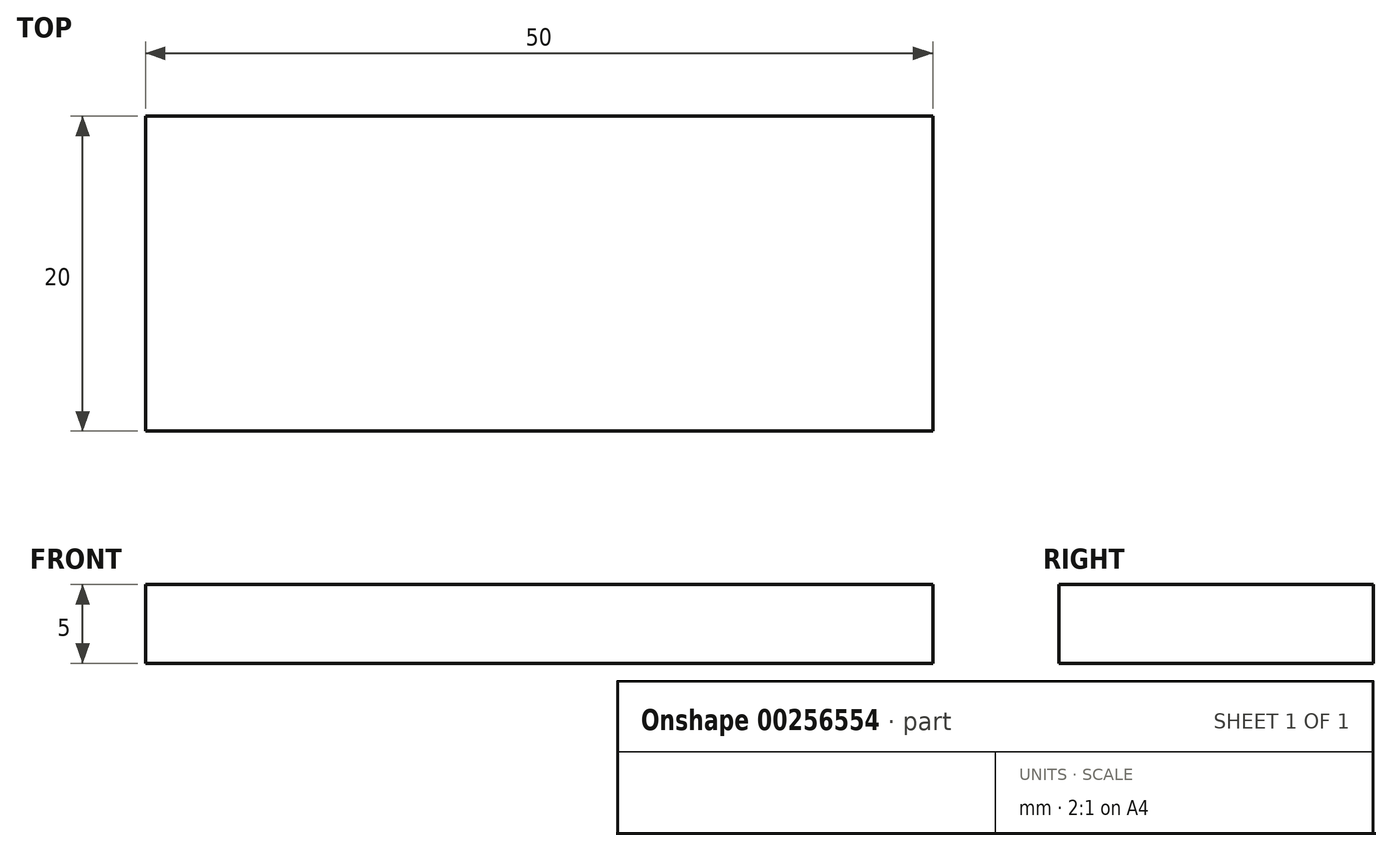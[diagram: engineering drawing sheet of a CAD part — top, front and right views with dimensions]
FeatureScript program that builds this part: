
annotation { "Feature Type Name" : "Feature", "Feature Type Description" : "" }
export const myFeature = defineFeature(function(context is Context, id is Id, definition is map)
    precondition{}
    {
        {
            var Q0;
            Q0=qCreatedBy(makeId("Top.planeOp"),FACE);
            var sketch = newSketch(context, id + "F0", { "sketchPlane" : qUnion([Q0])});
            skLineSegment(sketch, "E0.bottom", {"start": v(0, 0) * mm, "end": v(-50, 0) * mm});
            skLineSegment(sketch, "E0.top", {"start": v(0, 20) * mm, "end": v(-50, 20) * mm});
            skLineSegment(sketch, "E0.left", {"start": v(0, 0) * mm, "end": v(0, 20) * mm});
            skLineSegment(sketch, "E0.right", {"start": v(-50, 0) * mm, "end": v(-50, 20) * mm});
            skLineSegment(sketch, "E1", {"start": v(-50, 20) * mm, "end": v(0, 20) * mm, "construction": true});
            skLineSegment(sketch, "E2", {"start": v(-25, 20) * mm, "end": v(-25, 0) * mm, "construction": true});
            skLineSegment(sketch, "E3", {"start": v(-50, 10) * mm, "end": v(0, 10) * mm, "construction": true});
            skPoint(sketch, "E4", {"position": v(-25, 10) * mm});
            skLineSegment(sketch, "E5", {"start": v(-50, 20) * mm, "end": v(-50, 10) * mm});
            skPoint(sketch, "E6", {"position": v(-50, 15) * mm});
            skLineSegment(sketch, "E7", {"start": v(-50, 10) * mm, "end": v(-50, 0) * mm, "construction": true});
            skPoint(sketch, "E8", {"position": v(-50, 5) * mm});
            skSolve(sketch);
        }
        {
            var Q0;
            {var subQ12=sQuery(id+"F0.wireOp",EDGE,"E0.bottom");Q0=makeQuery(id+"F0.imprint","IMPRINT",FACE,{"disambiguationData":[TD([[makeQuery(id+"F0.imprint","IMPRINT",EDGE,{"derivedFrom":subQ12}),-1.0]])]});}
            var Q1;
            Q1=makeQuery(id+"F0.imprint","IMPRINT",FACE,{"disambiguationData":[TD([[makeQuery(id+"F0.imprint","IMPRINT",EDGE,{"derivedFrom":sQuery(id+"F0.wireOp",EDGE,"46239ded-874b-41ba-a554-3d8b998b9509.sketch_text.stroke-0")}),-1.0]])]});
            var Q2;
            Q2=makeQuery(id+"F0.imprint","IMPRINT",FACE,{"disambiguationData":[TD([[makeQuery(id+"F0.imprint","IMPRINT",EDGE,{"derivedFrom":sQuery(id+"F0.wireOp",EDGE,"46239ded-874b-41ba-a554-3d8b998b9509.sketch_text.stroke-145")}),-1.0]])]});
            var Q3;
            Q3=makeQuery(id+"F0.imprint","IMPRINT",FACE,{"disambiguationData":[TD([[makeQuery(id+"F0.imprint","IMPRINT",EDGE,{"derivedFrom":sQuery(id+"F0.wireOp",EDGE,"46239ded-874b-41ba-a554-3d8b998b9509.sketch_text.stroke-293")}),-1.0]])]});
            var Q4;
            Q4=makeQuery(id+"F0.imprint","IMPRINT",FACE,{"disambiguationData":[TD([[makeQuery(id+"F0.imprint","IMPRINT",EDGE,{"derivedFrom":sQuery(id+"F0.wireOp",EDGE,"46239ded-874b-41ba-a554-3d8b998b9509.sketch_text.stroke-276")}),-1.0]])]});
            var Q5;
            Q5=makeQuery(id+"F0.imprint","IMPRINT",FACE,{"disambiguationData":[TD([[makeQuery(id+"F0.imprint","IMPRINT",EDGE,{"derivedFrom":sQuery(id+"F0.wireOp",EDGE,"46239ded-874b-41ba-a554-3d8b998b9509.sketch_text.stroke-299")}),-1.0]])]});
            var Q6;
            Q6=makeQuery(id+"F0.imprint","IMPRINT",FACE,{"disambiguationData":[TD([[makeQuery(id+"F0.imprint","IMPRINT",EDGE,{"derivedFrom":sQuery(id+"F0.wireOp",EDGE,"46239ded-874b-41ba-a554-3d8b998b9509.sketch_text.stroke-111")}),1.0]])]});
            var Q7;
            Q7=makeQuery(id+"F0.imprint","IMPRINT",FACE,{"disambiguationData":[TD([[makeQuery(id+"F0.imprint","IMPRINT",EDGE,{"derivedFrom":sQuery(id+"F0.wireOp",EDGE,"46239ded-874b-41ba-a554-3d8b998b9509.sketch_text.stroke-237")}),-1.0]])]});
            var Q8;
            Q8=makeQuery(id+"F0.imprint","IMPRINT",FACE,{"disambiguationData":[TD([[makeQuery(id+"F0.imprint","IMPRINT",EDGE,{"derivedFrom":sQuery(id+"F0.wireOp",EDGE,"46239ded-874b-41ba-a554-3d8b998b9509.sketch_text.stroke-67")}),-1.0]])]});
            var Q9;
            {var subQ4=sQuery(id+"F0.wireOp",EDGE,"46239ded-874b-41ba-a554-3d8b998b9509.sketch_text.stroke-323");Q9=makeQuery(id+"F0.imprint","IMPRINT",FACE,{"disambiguationData":[TD([[makeQuery(id+"F0.imprint","IMPRINT",EDGE,{"derivedFrom":subQ4}),1.0]])]});}
            var Q10;
            Q10=makeQuery(id+"F0.imprint","IMPRINT",FACE,{"disambiguationData":[TD([[makeQuery(id+"F0.imprint","IMPRINT",EDGE,{"derivedFrom":sQuery(id+"F0.wireOp",EDGE,"46239ded-874b-41ba-a554-3d8b998b9509.sketch_text.stroke-314")}),-1.0]])]});
            var Q11;
            Q11=makeQuery(id+"F0.imprint","IMPRINT",FACE,{"disambiguationData":[TD([[makeQuery(id+"F0.imprint","IMPRINT",EDGE,{"derivedFrom":sQuery(id+"F0.wireOp",EDGE,"46239ded-874b-41ba-a554-3d8b998b9509.sketch_text.stroke-118")}),-1.0]])]});
            var Q12;
            Q12=makeQuery(id+"F0.imprint","IMPRINT",FACE,{"disambiguationData":[TD([[makeQuery(id+"F0.imprint","IMPRINT",EDGE,{"derivedFrom":sQuery(id+"F0.wireOp",EDGE,"46239ded-874b-41ba-a554-3d8b998b9509.sketch_text.stroke-173")}),-1.0]])]});
            var Q13;
            Q13=makeQuery(id+"F0.imprint","IMPRINT",FACE,{"disambiguationData":[TD([[makeQuery(id+"F0.imprint","IMPRINT",EDGE,{"derivedFrom":sQuery(id+"F0.wireOp",EDGE,"46239ded-874b-41ba-a554-3d8b998b9509.sketch_text.stroke-42")}),-1.0]])]});
            var Q14;
            {var subQ13=sQuery(id+"F0.wireOp",EDGE,"46239ded-874b-41ba-a554-3d8b998b9509.sketch_text.stroke-96");Q14=makeQuery(id+"F0.imprint","IMPRINT",FACE,{"disambiguationData":[TD([[makeQuery(id+"F0.imprint","IMPRINT",EDGE,{"derivedFrom":subQ13}),-1.0]])]});}
            var Q15;
            Q15=makeQuery(id+"F0.imprint","IMPRINT",FACE,{"disambiguationData":[TD([[makeQuery(id+"F0.imprint","IMPRINT",EDGE,{"derivedFrom":sQuery(id+"F0.wireOp",EDGE,"46239ded-874b-41ba-a554-3d8b998b9509.sketch_text.stroke-27")}),-1.0]])]});
            var Q16;
            Q16=makeQuery(id+"F0.imprint","IMPRINT",FACE,{"disambiguationData":[TD([[makeQuery(id+"F0.imprint","IMPRINT",EDGE,{"derivedFrom":sQuery(id+"F0.wireOp",EDGE,"46239ded-874b-41ba-a554-3d8b998b9509.sketch_text.stroke-254")}),-1.0]])]});
            var Q17;
            {var subQ0=sQuery(id+"F0.wireOp",EDGE,"46239ded-874b-41ba-a554-3d8b998b9509.sketch_text.stroke-271");Q17=makeQuery(id+"F0.imprint","IMPRINT",FACE,{"disambiguationData":[TD([[makeQuery(id+"F0.imprint","IMPRINT",EDGE,{"derivedFrom":subQ0}),1.0]])]});}
            var Q18;
            Q18=makeQuery(id+"F0.imprint","IMPRINT",FACE,{"disambiguationData":[TD([[makeQuery(id+"F0.imprint","IMPRINT",EDGE,{"derivedFrom":sQuery(id+"F0.wireOp",EDGE,"46239ded-874b-41ba-a554-3d8b998b9509.sketch_text.stroke-215")}),-1.0]])]});
            var Q19;
            {var subQ4=sQuery(id+"F0.wireOp",EDGE,"46239ded-874b-41ba-a554-3d8b998b9509.sketch_text.stroke-232");Q19=makeQuery(id+"F0.imprint","IMPRINT",FACE,{"disambiguationData":[TD([[makeQuery(id+"F0.imprint","IMPRINT",EDGE,{"derivedFrom":subQ4}),1.0]])]});}
            var Q20;
            Q20=makeQuery(id+"F0.imprint","IMPRINT",FACE,{"disambiguationData":[TD([[makeQuery(id+"F0.imprint","IMPRINT",EDGE,{"derivedFrom":sQuery(id+"F0.wireOp",EDGE,"46239ded-874b-41ba-a554-3d8b998b9509.sketch_text.stroke-21")}),-1.0]])]});
            var Q21;
            {var subQ1=sQuery(id+"F0.wireOp",EDGE,"46239ded-874b-41ba-a554-3d8b998b9509.sketch_text.stroke-94");var subQ5=sQuery(id+"F0.wireOp",EDGE,"46239ded-874b-41ba-a554-3d8b998b9509.sketch_text.stroke-95");var subQ6=makeQuery(id+"F0.imprint","INTERSECT",VERTEX,{"derivedFrom":[subQ1,subQ5]});Q21=makeQuery(id+"F0.imprint","IMPRINT",FACE,{"disambiguationData":[TD([[makeQuery(id+"F0.imprint","IMPRINT",EDGE,{"disambiguationData":[TD([[subQ6,1.0]])],"derivedFrom":subQ1}),-1.0]])]});}
            var Q22;
            {var subQ0=sQuery(id+"F0.wireOp",EDGE,"Q8oznGCK-WREW-ciFv-OXbm-MldBUsIqsDus");var subQ1=sQuery(id+"F0.wireOp",EDGE,"46239ded-874b-41ba-a554-3d8b998b9509.sketch_text.stroke-116");var subQ2=makeQuery(id+"F0.imprint","INTERSECT",VERTEX,{"disambiguationData":[OD(0.0)],"derivedFrom":[subQ1,subQ0]});Q22=makeQuery(id+"F0.imprint","IMPRINT",FACE,{"disambiguationData":[TD([[makeQuery(id+"F0.imprint","IMPRINT",EDGE,{"disambiguationData":[TD([[subQ2,-1.0]])],"derivedFrom":subQ1}),1.0]])]});}
            var Q23;
            {var subQ0=sQuery(id+"F0.wireOp",EDGE,"46239ded-874b-41ba-a554-3d8b998b9509.sketch_text.stroke-110");var subQ1=sQuery(id+"F0.wireOp",EDGE,"46239ded-874b-41ba-a554-3d8b998b9509.sketch_text.stroke-94");var subQ2=makeQuery(id+"F0.imprint","INTERSECT",VERTEX,{"derivedFrom":[subQ1,subQ0]});Q23=makeQuery(id+"F0.imprint","IMPRINT",FACE,{"disambiguationData":[TD([[makeQuery(id+"F0.imprint","IMPRINT",EDGE,{"disambiguationData":[TD([[subQ2,-1.0]])],"derivedFrom":subQ1}),1.0]])]});}
            var Q24;
            {var subQ0=sQuery(id+"F0.wireOp",EDGE,"Q8oznGCK-WREW-ciFv-OXbm-MldBUsIqsDus");var subQ1=sQuery(id+"F0.wireOp",EDGE,"46239ded-874b-41ba-a554-3d8b998b9509.sketch_text.stroke-110");var subQ2=makeQuery(id+"F0.imprint","INTERSECT",VERTEX,{"disambiguationData":[OD(0.0)],"derivedFrom":[subQ1,subQ0]});Q24=makeQuery(id+"F0.imprint","IMPRINT",FACE,{"disambiguationData":[TD([[makeQuery(id+"F0.imprint","IMPRINT",EDGE,{"disambiguationData":[TD([[subQ2,-1.0]])],"derivedFrom":subQ1}),-1.0]])]});}
            var Q25;
            {var subQ1=sQuery(id+"F0.wireOp",EDGE,"46239ded-874b-41ba-a554-3d8b998b9509.sketch_text.stroke-94");var subQ5=sQuery(id+"F0.wireOp",EDGE,"46239ded-874b-41ba-a554-3d8b998b9509.sketch_text.stroke-95");var subQ6=makeQuery(id+"F0.imprint","INTERSECT",VERTEX,{"derivedFrom":[subQ1,subQ5]});Q25=makeQuery(id+"F0.imprint","IMPRINT",FACE,{"disambiguationData":[TD([[makeQuery(id+"F0.imprint","IMPRINT",EDGE,{"disambiguationData":[TD([[subQ6,1.0]])],"derivedFrom":subQ1}),1.0]])]});}
            var Q26;
            {var subQ5=sQuery(id+"F0.wireOp",EDGE,"0Cm8tG60-S02J-i4aP-JSc0-yH27m7YXlth4");Q26=makeQuery(id+"F0.imprint","IMPRINT",FACE,{"disambiguationData":[TD([[makeQuery(id+"F0.imprint","IMPRINT",EDGE,{"derivedFrom":subQ5}),-1.0]])]});}
            var Q27;
            {var subQ0=sQuery(id+"F0.wireOp",EDGE,"65ef3425-be18-4a71-846c-047fe40a4213");var subQ1=sQuery(id+"F0.wireOp",EDGE,"46239ded-874b-41ba-a554-3d8b998b9509.sketch_text.stroke-227");var subQ2=makeQuery(id+"F0.imprint","INTERSECT",VERTEX,{"derivedFrom":[subQ1,subQ0]});Q27=makeQuery(id+"F0.imprint","IMPRINT",FACE,{"disambiguationData":[TD([[makeQuery(id+"F0.imprint","IMPRINT",EDGE,{"disambiguationData":[TD([[subQ2,-1.0]])],"derivedFrom":subQ1}),-1.0]])]});}
            var Q28;
            {var subQ0=sQuery(id+"F0.wireOp",EDGE,"gtB94JM7-yXso-rpJw-vOx3-gdZZ2Ft0KCr5");var subQ6=sQuery(id+"F0.wireOp",EDGE,"46239ded-874b-41ba-a554-3d8b998b9509.sketch_text.stroke-266");var subQ9=makeQuery(id+"F0.imprint","INTERSECT",VERTEX,{"derivedFrom":[subQ6,subQ0]});Q28=makeQuery(id+"F0.imprint","IMPRINT",FACE,{"disambiguationData":[TD([[makeQuery(id+"F0.imprint","IMPRINT",EDGE,{"disambiguationData":[TD([[subQ9,-1.0]])],"derivedFrom":subQ6}),-1.0]])]});}
            var Q29;
            {var subQ5=sQuery(id+"F0.wireOp",EDGE,"4ef20cd8-9e43-47db-a2b0-4fcc56ceea7b");Q29=makeQuery(id+"F0.imprint","IMPRINT",FACE,{"disambiguationData":[TD([[makeQuery(id+"F0.imprint","IMPRINT",EDGE,{"derivedFrom":subQ5}),-1.0]])]});}
            var Q30;
            {var subQ1=sQuery(id+"F0.wireOp",EDGE,"332cb5a9-6c62-4834-ad55-cdc3ae7c4fdb");var subQ9=sQuery(id+"F0.wireOp",EDGE,"46239ded-874b-41ba-a554-3d8b998b9509.sketch_text.stroke-317");var subQ10=makeQuery(id+"F0.imprint","INTERSECT",VERTEX,{"derivedFrom":[subQ9,subQ1]});Q30=makeQuery(id+"F0.imprint","IMPRINT",FACE,{"disambiguationData":[TD([[makeQuery(id+"F0.imprint","IMPRINT",EDGE,{"disambiguationData":[TD([[subQ10,-1.0]])],"derivedFrom":subQ9}),-1.0]])]});}
            var Q31;
            {var subQ0=sQuery(id+"F0.wireOp",EDGE,"332cb5a9-6c62-4834-ad55-cdc3ae7c4fdb");var subQ1=sQuery(id+"F0.wireOp",EDGE,"46239ded-874b-41ba-a554-3d8b998b9509.sketch_text.stroke-322");var subQ2=makeQuery(id+"F0.imprint","INTERSECT",VERTEX,{"disambiguationData":[OD(0.0)],"derivedFrom":[subQ1,subQ0]});Q31=makeQuery(id+"F0.imprint","IMPRINT",FACE,{"disambiguationData":[TD([[makeQuery(id+"F0.imprint","IMPRINT",EDGE,{"disambiguationData":[TD([[subQ2,-1.0]])],"derivedFrom":subQ1}),1.0]])]});}
            var Q32;
            {var subQ5=sQuery(id+"F0.wireOp",EDGE,"77af4e2e-d80d-4f87-98c3-e9a24f769475");Q32=makeQuery(id+"F0.imprint","IMPRINT",FACE,{"disambiguationData":[TD([[makeQuery(id+"F0.imprint","IMPRINT",EDGE,{"derivedFrom":subQ5}),-1.0]])]});}
            var Q33;
            {var subQ0=sQuery(id+"F0.wireOp",EDGE,"332cb5a9-6c62-4834-ad55-cdc3ae7c4fdb");var subQ1=sQuery(id+"F0.wireOp",EDGE,"46239ded-874b-41ba-a554-3d8b998b9509.sketch_text.stroke-317");var subQ2=makeQuery(id+"F0.imprint","INTERSECT",VERTEX,{"derivedFrom":[subQ1,subQ0]});Q33=makeQuery(id+"F0.imprint","IMPRINT",FACE,{"disambiguationData":[TD([[makeQuery(id+"F0.imprint","IMPRINT",EDGE,{"disambiguationData":[TD([[subQ2,-1.0]])],"derivedFrom":subQ1}),1.0]])]});}
            var Q34;
            {var subQ0=sQuery(id+"F0.wireOp",EDGE,"gtB94JM7-yXso-rpJw-vOx3-gdZZ2Ft0KCr5");var subQ1=sQuery(id+"F0.wireOp",EDGE,"46239ded-874b-41ba-a554-3d8b998b9509.sketch_text.stroke-266");var subQ2=makeQuery(id+"F0.imprint","INTERSECT",VERTEX,{"derivedFrom":[subQ1,subQ0]});Q34=makeQuery(id+"F0.imprint","IMPRINT",FACE,{"disambiguationData":[TD([[makeQuery(id+"F0.imprint","IMPRINT",EDGE,{"disambiguationData":[TD([[subQ2,-1.0]])],"derivedFrom":subQ1}),1.0]])]});}
            var Q35;
            {var subQ0=sQuery(id+"F0.wireOp",EDGE,"46239ded-874b-41ba-a554-3d8b998b9509.sketch_text.stroke-327");var subQ1=sQuery(id+"F0.wireOp",EDGE,"46239ded-874b-41ba-a554-3d8b998b9509.sketch_text.stroke-322");var subQ2=makeQuery(id+"F0.imprint","INTERSECT",VERTEX,{"derivedFrom":[subQ1,subQ0]});Q35=makeQuery(id+"F0.imprint","IMPRINT",FACE,{"disambiguationData":[TD([[makeQuery(id+"F0.imprint","IMPRINT",EDGE,{"disambiguationData":[TD([[subQ2,-1.0]])],"derivedFrom":subQ1}),-1.0]])]});}
            var Q36;
            {var subQ0=sQuery(id+"F0.wireOp",EDGE,"c73ebb9b-1a12-49aa-a605-e1df585d36d80.MirrorCS");var subQ1=sQuery(id+"F0.wireOp",EDGE,"46239ded-874b-41ba-a554-3d8b998b9509.sketch_text.stroke-327");var subQ2=makeQuery(id+"F0.imprint","INTERSECT",VERTEX,{"disambiguationData":[OD(0.0)],"derivedFrom":[subQ1,subQ0]});Q36=makeQuery(id+"F0.imprint","IMPRINT",FACE,{"disambiguationData":[TD([[makeQuery(id+"F0.imprint","IMPRINT",EDGE,{"disambiguationData":[TD([[subQ2,-1.0]])],"derivedFrom":subQ1}),1.0]])]});}
            extrude(context, id + "F1", {"entities" : qUnion([Q0, Q1, Q2, Q3, Q4, Q5, Q6, Q7, Q8, Q9, Q10, Q11, Q12, Q13, Q14, Q15, Q16, Q17, Q18, Q19, Q20, Q21, Q22, Q23, Q24, Q25, Q26, Q27, Q28, Q29, Q30, Q31, Q32, Q33, Q34, Q35, Q36]), "endBound" : BoundingType.SYMMETRIC, "depth" : 5 * mm});
        }
    });
